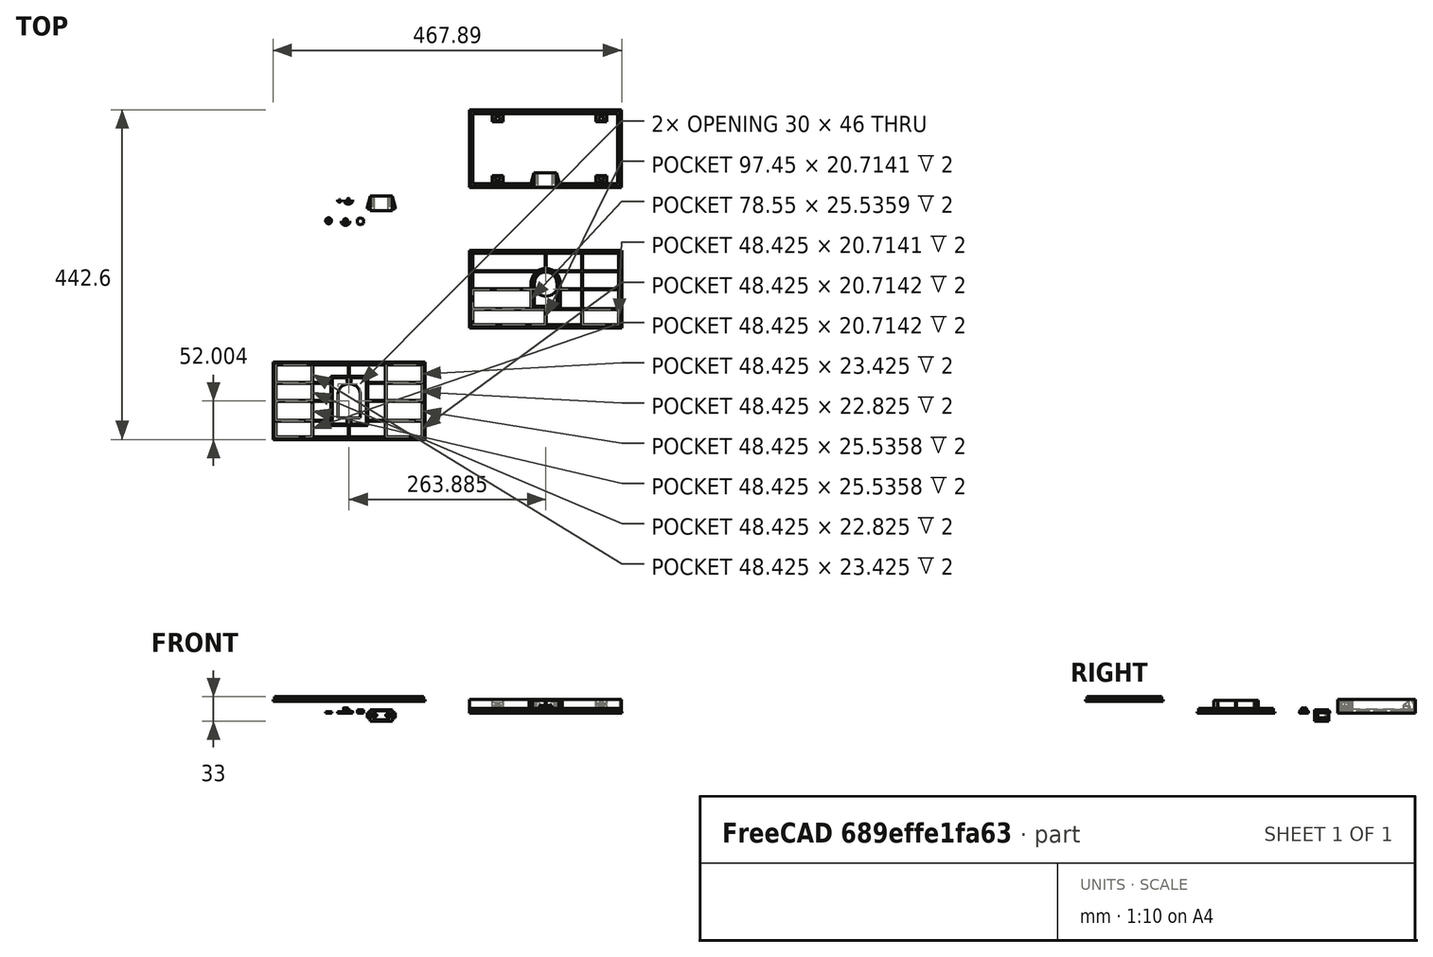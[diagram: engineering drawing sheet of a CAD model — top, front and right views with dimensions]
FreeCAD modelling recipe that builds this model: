
FCSTD DOCUMENT  (FreeCAD 0.18.3R)
Label: lamp.base.template
License: All rights reserved
LicenseURL: http://en.wikipedia.org/wiki/All_rights_reserved
objects: Part::Extrusion×114, Part::Part2DObjectPython×79, Part::Cut×50, Part::MultiFuse×34, Part::Feature×31, Part::Cone×2
note: 310 computed .brp shape members not serialized (recipe doc carries the construction recipe); baked Part::Feature solids carry a one-line shape summary decoded from their .brp

FEATURE [Part::Part2DObjectPython] Rectangle071  # Draft 2D object (typed FeaturePython)
  ChamferSize = 0
  Columns = 1
  FilletRadius = 0
  Height = 100.5
  Length = 200.5
  MakeFace = true
  Placement = pos=(-212.48,-326.495,-1) rot=(0,0,1;0rad)
  Rows = 1
FEATURE [Part::Part2DObjectPython] Rectangle072  # Draft 2D object (typed FeaturePython)
  ChamferSize = 0
  Columns = 1
  FilletRadius = 0
  Height = 104
  Length = 204
  MakeFace = true
  Placement = pos=(-214.23,-328.245,-1) rot=(0,0,1;0rad)
  Rows = 1
  Support = -> [Rectangle071]
FEATURE [Part::Extrusion] Extrude098
  Base = -> Rectangle071
  Dir = (0,2e-16,1)
  DirMode = 2
  FaceMakerClass = Part::FaceMakerBullseye
  LengthFwd = 16
  LengthRev = 0
  Solid = false
  Symmetric = false
FEATURE [Part::Extrusion] Extrude099
  Base = -> Rectangle072
  Dir = (0,2e-16,1)
  DirMode = 2
  FaceMakerClass = Part::FaceMakerBullseye
  LengthFwd = 16
  LengthRev = 0
  Solid = false
  Symmetric = false
FEATURE [Part::Cut] Cut027
  Base = -> Extrude099
  Tool = -> Extrude098
FEATURE [Part::Part2DObjectPython] Rectangle073  # Draft 2D object (typed FeaturePython)
  ChamferSize = 0
  Columns = 1
  FilletRadius = 0
  Height = 100.5
  Length = 200.5
  MakeFace = true
  Placement = pos=(-212.48,-326.495,-1) rot=(0,0,1;0rad)
  Rows = 1
FEATURE [Part::Extrusion] Extrude100
  Base = -> Rectangle073
  Dir = (0,2e-16,1)
  DirMode = 2
  FaceMakerClass = Part::FaceMakerBullseye
  LengthFwd = 2
  LengthRev = 0
  Placement = pos=(0,0,1) rot=(0,0,1;0rad)
  Solid = false
  Symmetric = false
FEATURE [Part::Part2DObjectPython] Rectangle074  # Draft 2D object (typed FeaturePython)
  ChamferSize = 0
  Columns = 1
  FilletRadius = 0
  Height = 96
  Length = 196
  MakeFace = true
  Placement = pos=(-210.23,-324.245,4.41e-14) rot=(0,0,1;0rad)
  Rows = 1
FEATURE [Part::Extrusion] Extrude101
  Base = -> Rectangle074
  Dir = (0,2e-16,1)
  DirMode = 2
  FaceMakerClass = Part::FaceMakerBullseye
  LengthFwd = 10
  LengthRev = 0
  Solid = false
  Symmetric = false
FEATURE [Part::Cut] Cut028
  Base = -> Extrude100
  Tool = -> Extrude101
FEATURE [Part::Feature] Face
  shape: bbox 204 x 104 x 2e-07 mm, 1 faces, 0 solids (baked)
FEATURE [Part::Extrusion] Extrusion001
  Base = -> Face
  Dir = (0,-5e-16,-2)
  DirMode = 0
  FaceMakerClass = Part::FaceMakerBullseye
  LengthFwd = 0
  LengthRev = 0
  Solid = true
  Symmetric = false
FEATURE [Part::Feature] Face001
  shape: bbox 3e-07 x 96 x 2 mm, 1 faces, 0 solids (baked)
FEATURE [Part::Extrusion] Extrusion002
  Base = -> Face001
  Dir = (1,0,0)
  DirMode = 0
  FaceMakerClass = Part::FaceMakerBullseye
  LengthFwd = 0
  LengthRev = 0
  Solid = true
  Symmetric = false
FEATURE [Part::Feature] Face002
  shape: bbox 196 x 3e-07 x 2 mm, 1 faces, 0 solids (baked)
FEATURE [Part::Extrusion] Extrusion003
  Base = -> Face002
  Dir = (0,1,-2e-16)
  DirMode = 0
  FaceMakerClass = Part::FaceMakerBullseye
  LengthFwd = 0
  LengthRev = 0
  Solid = true
  Symmetric = false
FEATURE [Part::Feature] Face003
  shape: bbox 3e-07 x 96 x 2 mm, 1 faces, 0 solids (baked)
FEATURE [Part::Extrusion] Extrusion004
  Base = -> Face003
  Dir = (-1,0,0)
  DirMode = 0
  FaceMakerClass = Part::FaceMakerBullseye
  LengthFwd = 0
  LengthRev = 0
  Solid = true
  Symmetric = false
FEATURE [Part::Feature] Face004
  shape: bbox 196 x 3e-07 x 2 mm, 1 faces, 0 solids (baked)
FEATURE [Part::Extrusion] Extrusion005
  Base = -> Face004
  Dir = (0,-1,2e-16)
  DirMode = 0
  FaceMakerClass = Part::FaceMakerBullseye
  LengthFwd = 0
  LengthRev = 0
  Solid = true
  Symmetric = false
FEATURE [Part::MultiFuse] Fusion022
  Shapes = -> [Extrusion003,Extrusion004,Extrusion002,Extrusion005]
FEATURE [Part::MultiFuse] Fusion023
  Shapes = -> [Extrusion001,Cut027]
FEATURE [Part::MultiFuse] Fusion024
  Shapes = -> [Fusion023,Fusion022]
FEATURE [Part::Part2DObjectPython] Rectangle085  # Draft 2D object (typed FeaturePython)
  ChamferSize = 0
  Columns = 1
  FilletRadius = 0
  Height = 96.1
  Length = 196.1
  MakeFace = true
  Placement = pos=(-211.308,-540.059,-3) rot=(0,0,1;0rad)
  Rows = 1
FEATURE [Part::Part2DObjectPython] Rectangle086  # Draft 2D object (typed FeaturePython)
  ChamferSize = 0
  Columns = 1
  FilletRadius = 0
  Height = 104
  Length = 204
  MakeFace = true
  Placement = pos=(-215.258,-544.009,-3) rot=(0,0,1;0rad)
  Rows = 1
FEATURE [Part::Extrusion] Extrude120
  Base = -> Rectangle086
  Dir = (0,2e-16,1)
  DirMode = 2
  FaceMakerClass = Part::FaceMakerBullseye
  LengthFwd = 2
  LengthRev = 0
  Placement = pos=(-4.3e-14,5.7e-14,-6) rot=(0,0,1;0rad)
  Solid = false
  Symmetric = false
FEATURE [Part::Part2DObjectPython] Rectangle087  # Draft 2D object (typed FeaturePython)
  ChamferSize = 0
  Columns = 1
  FilletRadius = 0
  Height = 100.1
  Length = 200.1
  MakeFace = true
  Placement = pos=(-213.308,-542.059,-3) rot=(0,0,1;0rad)
  Rows = 1
  Support = -> [Rectangle085]
FEATURE [Part::Extrusion] Extrude121
  Base = -> Rectangle087
  Dir = (0,0,1)
  DirMode = 2
  FaceMakerClass = Part::FaceMakerBullseye
  LengthFwd = -4
  LengthRev = 0
  Solid = false
  Symmetric = false
FEATURE [Part::Extrusion] Extrude122
  Base = -> Rectangle085
  Dir = (0,0,1)
  DirMode = 2
  FaceMakerClass = Part::FaceMakerBullseye
  LengthFwd = -4
  LengthRev = 0
  Solid = false
  Symmetric = false
FEATURE [Part::Cut] Cut035
  Base = -> Extrude121
  Tool = -> Extrude122
FEATURE [Part::Part2DObjectPython] Rectangle088  # Draft 2D object (typed FeaturePython)
  ChamferSize = 0
  Columns = 1
  FilletRadius = 0
  Height = 1.2
  Length = 196.1
  MakeFace = true
  Placement = pos=(-211.308,-492.009,-3) rot=(0,0,1;0rad)
  Rows = 1
FEATURE [Part::Part2DObjectPython] Rectangle089  # Draft 2D object (typed FeaturePython)
  ChamferSize = 0
  Columns = 1
  FilletRadius = 0
  Height = 96.1
  Length = 1.2
  MakeFace = true
  Placement = pos=(-113.858,-443.959,-3) rot=(1,0,0;3.14159rad)
  Rows = 1
  Support = -> [Cut035]
FEATURE [Part::Part2DObjectPython] Rectangle090  # Draft 2D object (typed FeaturePython)
  ChamferSize = 0
  Columns = 1
  FilletRadius = 0
  Height = 1.2
  Length = 196.1
  MakeFace = true
  Placement = pos=(-211.308,-467.384,-3) rot=(1,0,0;3.14159rad)
  Rows = 1
FEATURE [Part::Part2DObjectPython] Rectangle091  # Draft 2D object (typed FeaturePython)
  ChamferSize = 0
  Columns = 1
  FilletRadius = 0
  Height = 1.2
  Length = 196.1
  MakeFace = true
  Placement = pos=(-211.308,-518.145,-3) rot=(1,0,0;3.14159rad)
  Rows = 1
FEATURE [Part::Part2DObjectPython] Rectangle092  # Draft 2D object (typed FeaturePython)
  ChamferSize = 0
  Columns = 1
  FilletRadius = 0
  Height = 96.1
  Length = 1.2
  MakeFace = true
  Placement = pos=(-64.8332,-443.959,-3) rot=(1,0,0;3.14159rad)
  Rows = 1
FEATURE [Part::Extrusion] Extrude123
  Base = -> Rectangle090
  Dir = (0,-2e-16,-1)
  DirMode = 2
  FaceMakerClass = Part::FaceMakerBullseye
  LengthFwd = 2
  LengthRev = 0
  Placement = pos=(-2.8e-14,0,-2) rot=(0,0,1;0rad)
  Solid = false
  Symmetric = false
FEATURE [Part::Extrusion] Extrude124
  Base = -> Rectangle092
  Dir = (0,-2e-16,-1)
  DirMode = 2
  FaceMakerClass = Part::FaceMakerBullseye
  LengthFwd = 2
  LengthRev = 0
  Placement = pos=(-2.8e-14,0,-2) rot=(0,0,1;0rad)
  Solid = false
  Symmetric = false
FEATURE [Part::Extrusion] Extrude125
  Base = -> Rectangle088
  Dir = (0,2e-16,1)
  DirMode = 2
  FaceMakerClass = Part::FaceMakerBullseye
  LengthFwd = -2
  LengthRev = 0
  Placement = pos=(-2.8e-14,-0.6,-2) rot=(0,0,1;0rad)
  Solid = false
  Symmetric = false
FEATURE [Part::Extrusion] Extrude126
  Base = -> Rectangle091
  Dir = (0,-2e-16,-1)
  DirMode = 2
  FaceMakerClass = Part::FaceMakerBullseye
  LengthFwd = 2
  LengthRev = 0
  Placement = pos=(-2.8e-14,0,-2) rot=(0,0,1;0rad)
  Solid = false
  Symmetric = false
FEATURE [Part::Extrusion] Extrude127
  Base = -> Rectangle089
  Dir = (0,0,-1)
  DirMode = 2
  FaceMakerClass = Part::FaceMakerBullseye
  LengthFwd = 2
  LengthRev = 0
  Placement = pos=(-2.8e-14,0,-2) rot=(0,0,1;0rad)
  Solid = false
  Symmetric = false
FEATURE [Part::Part2DObjectPython] Circle022  # Draft 2D object (typed FeaturePython)
  FirstAngle = 0
  LastAngle = 0
  MakeFace = true
  Placement = pos=(-130.429,-169.951,7.33959) rot=(1,0,0;3.14157rad)
  Radius = 6
FEATURE [Part::Part2DObjectPython] Circle023  # Draft 2D object (typed FeaturePython)
  FirstAngle = 0
  LastAngle = 0
  MakeFace = true
  Placement = pos=(-130.429,-169.951,7.33959) rot=(-1,0,0;2.2e-05rad)
  Radius = 2.5
FEATURE [Part::Part2DObjectPython] Circle  # Draft 2D object (typed FeaturePython)
  FirstAngle = 0
  LastAngle = 0
  MakeFace = true
  Placement = pos=(-130.429,-169.95,12.3396) rot=(-1,0,0;2.2e-05rad)
  Radius = 3
FEATURE [Part::Extrusion] Extrude142
  Base = -> Circle
  Dir = (0,2.19278e-05,1)
  DirMode = 2
  FaceMakerClass = Part::FaceMakerBullseye
  LengthFwd = -2.5
  LengthRev = 0
  Solid = false
  Symmetric = false
FEATURE [Part::Part2DObjectPython] Rectangle104  # Draft 2D object (typed FeaturePython)
  ChamferSize = 0
  Columns = 1
  FilletRadius = 0
  Height = 2
  Length = 6
  MakeFace = true
  Placement = pos=(-133.429,-170.95,12.3396) rot=(-1,0,0;2.2e-05rad)
  Rows = 1
  Support = -> [Extrude142]
FEATURE [Part::Cone] Cone002
  Angle = 360
  AttacherType = Attacher::AttachEngine3D
  Height = 10
  Placement = pos=(-126.434,-151.902,12.3392) rot=(0,0,1;0rad)
  Radius1 = 6
  Radius2 = 3
FEATURE [Part::Cone] Cone
  Angle = 360
  AttacherType = Attacher::AttachEngine3D
  Height = 10
  Placement = pos=(-126.434,-151.902,12.3392) rot=(0,0,1;0rad)
  Radius1 = 5
  Radius2 = 0
FEATURE [Part::Cut] Cut048
  Base = -> Cone002
  Placement = pos=(-3.99517,-18.0483,-4.4996) rot=(0,0,1;0rad)
  Tool = -> Cone
FEATURE [Part::Part2DObjectPython] Wire005  # Draft 2D object (typed FeaturePython)
  ChamferSize = 0
  Closed = true
  End = (-172.23,-313.495,6)
  FilletRadius = 0
  Length = 29.8885
  MakeFace = true
  Placement = pos=(-176.23,-311.495,6) rot=(0,0,1;0rad)
  Points = (6) [(0,0,0),(-4,-2,-1.77636e-15),(-4,-8,0),(0,-10,0),(4,-8,8.88178e-16),(4,-2,1.77636e-15)]
  Start = (-176.23,-311.495,6)
  Subdivisions = 0
FEATURE [Part::Extrusion] Extrude148
  Base = -> Wire005
  Dir = (0,0,1)
  DirMode = 2
  FaceMakerClass = Part::FaceMakerBullseye
  LengthFwd = 4.4
  LengthRev = 0
  Placement = pos=(139.25,80.4695,-4) rot=(0,0,1;0rad)
  Solid = false
  Symmetric = false
FEATURE [Part::Part2DObjectPython] Rectangle  # Draft 2D object (typed FeaturePython)
  ChamferSize = 0
  Columns = 1
  FilletRadius = 0
  Height = 14
  Length = 15
  MakeFace = true
  Placement = pos=(-183.73,-326.495,6) rot=(0,0,1;0rad)
  Rows = 1
FEATURE [Part::Extrusion] Extrude149
  Base = -> Wire005
  Dir = (0,0,1)
  DirMode = 2
  FaceMakerClass = Part::FaceMakerBullseye
  LengthFwd = 4.4
  LengthRev = 0
  Placement = pos=(71.3743,-83.0439,-15) rot=(0,0,1;0rad)
  Solid = false
  Symmetric = false
FEATURE [Part::Extrusion] Extrude150
  Base = -> Wire005
  Dir = (0,0,1)
  DirMode = 2
  FaceMakerClass = Part::FaceMakerBullseye
  LengthFwd = 4.4
  LengthRev = 0
  Placement = pos=(-2.8e-14,0,-4) rot=(0,0,1;0rad)
  Solid = false
  Symmetric = false
FEATURE [Part::Extrusion] Extrude151
  Base = -> Wire005
  Dir = (0,0,1)
  DirMode = 2
  FaceMakerClass = Part::FaceMakerBullseye
  LengthFwd = 4.4
  LengthRev = 0
  Placement = pos=(-2.8e-14,80.4695,-4) rot=(0,0,1;0rad)
  Solid = false
  Symmetric = false
FEATURE [Part::Extrusion] Extrude152
  Base = -> Wire005
  Dir = (0,0,1)
  DirMode = 2
  FaceMakerClass = Part::FaceMakerBullseye
  LengthFwd = 4.4
  LengthRev = 0
  Placement = pos=(139.25,0,-4) rot=(0,0,1;0rad)
  Solid = false
  Symmetric = false
FEATURE [Part::Part2DObjectPython] Circle024  # Draft 2D object (typed FeaturePython)
  FirstAngle = 0
  LastAngle = 0
  MakeFace = true
  Placement = pos=(-176.23,-316.495,1.32e-13) rot=(1,0,0;3.14159rad)
  Radius = 2.8
FEATURE [Part::Extrusion] Extrude
  Base = -> Circle024
  Dir = (0,0,-1)
  DirMode = 2
  FaceMakerClass = Part::FaceMakerBullseye
  LengthFwd = -6.4
  LengthRev = 0
  Solid = false
  Symmetric = false
FEATURE [Part::Part2DObjectPython] Circle025  # Draft 2D object (typed FeaturePython)
  FirstAngle = 0
  LastAngle = 0
  MakeFace = true
  Placement = pos=(-176.23,-236.025,2.3e-14) rot=(1,0,0;3.14159rad)
  Radius = 2.8
  Support = -> [Extrude]
FEATURE [Part::Extrusion] Extrude153
  Base = -> Circle025
  Dir = (0,0,-1)
  DirMode = 2
  FaceMakerClass = Part::FaceMakerBullseye
  LengthFwd = -6.4
  LengthRev = 0
  Solid = false
  Symmetric = false
FEATURE [Part::Part2DObjectPython] Circle026  # Draft 2D object (typed FeaturePython)
  FirstAngle = 0
  LastAngle = 0
  MakeFace = true
  Placement = pos=(-36.9799,-316.495,2.5e-14) rot=(1,0,0;3.14159rad)
  Radius = 2.8
FEATURE [Part::Extrusion] Extrude154
  Base = -> Circle026
  Dir = (0,0,-1)
  DirMode = 2
  FaceMakerClass = Part::FaceMakerBullseye
  LengthFwd = -6.4
  LengthRev = 0
  Solid = false
  Symmetric = false
FEATURE [Part::Part2DObjectPython] Circle027  # Draft 2D object (typed FeaturePython)
  FirstAngle = 0
  LastAngle = 0
  MakeFace = true
  Placement = pos=(-36.9799,-236.025,2.5e-14) rot=(1,0,0;3.14159rad)
  Radius = 2.8
FEATURE [Part::Extrusion] Extrude155
  Base = -> Circle027
  Dir = (0,0,-1)
  DirMode = 2
  FaceMakerClass = Part::FaceMakerBullseye
  LengthFwd = -6.4
  LengthRev = 0
  Solid = false
  Symmetric = false
FEATURE [Part::Part2DObjectPython] Rectangle105  # Draft 2D object (typed FeaturePython)
  ChamferSize = 0
  Columns = 1
  FilletRadius = 0
  Height = 14
  Length = 15
  MakeFace = true
  Placement = pos=(-44.4799,-326.495,6) rot=(0,0,1;0rad)
  Rows = 1
FEATURE [Part::Part2DObjectPython] Rectangle106  # Draft 2D object (typed FeaturePython)
  ChamferSize = 0
  Columns = 1
  FilletRadius = 0
  Height = 14.0305
  Length = 15
  MakeFace = true
  Placement = pos=(-44.4799,-240.025,6) rot=(0,0,1;0rad)
  Rows = 1
FEATURE [Part::Part2DObjectPython] Rectangle107  # Draft 2D object (typed FeaturePython)
  ChamferSize = 0
  Columns = 1
  FilletRadius = 0
  Height = 14.0305
  Length = 15
  MakeFace = true
  Placement = pos=(-183.73,-240.025,6) rot=(0,0,1;0rad)
  Rows = 1
FEATURE [Part::Extrusion] Extrude156
  Base = -> Rectangle106
  Dir = (0,0,1)
  DirMode = 2
  FaceMakerClass = Part::FaceMakerBullseye
  LengthFwd = -6.4
  LengthRev = 0
  Placement = pos=(0,0,0.4) rot=(0,0,1;0rad)
  Solid = false
  Symmetric = false
FEATURE [Part::Extrusion] Extrude157
  Base = -> Rectangle107
  Dir = (0,0,1)
  DirMode = 2
  FaceMakerClass = Part::FaceMakerBullseye
  LengthFwd = -6.4
  LengthRev = 0
  Placement = pos=(0,0,0.4) rot=(0,0,1;0rad)
  Solid = false
  Symmetric = false
FEATURE [Part::Extrusion] Extrude158
  Base = -> Rectangle
  Dir = (0,0,1)
  DirMode = 2
  FaceMakerClass = Part::FaceMakerBullseye
  LengthFwd = -6.4
  LengthRev = 0
  Placement = pos=(0,0,0.4) rot=(0,0,1;0rad)
  Solid = false
  Symmetric = false
FEATURE [Part::Extrusion] Extrude159
  Base = -> Rectangle105
  Dir = (0,0,1)
  DirMode = 2
  FaceMakerClass = Part::FaceMakerBullseye
  LengthFwd = -6.4
  LengthRev = 0
  Placement = pos=(0,0,0.4) rot=(0,0,1;0rad)
  Solid = false
  Symmetric = false
FEATURE [Part::Cut] Cut050
  Base = -> Extrude159
  Tool = -> Extrude152
FEATURE [Part::Cut] Cut051
  Base = -> Cut050
  Tool = -> Extrude154
FEATURE [Part::Cut] Cut052
  Base = -> Extrude158
  Tool = -> Extrude150
FEATURE [Part::Cut] Cut053
  Base = -> Cut052
  Tool = -> Extrude
FEATURE [Part::Cut] Cut054
  Base = -> Extrude157
  Tool = -> Extrude151
FEATURE [Part::Cut] Cut055
  Base = -> Cut054
  Tool = -> Extrude153
FEATURE [Part::Cut] Cut056
  Base = -> Extrude156
  Tool = -> Extrude148
FEATURE [Part::Cut] Cut057
  Base = -> Cut056
  Tool = -> Extrude155
FEATURE [Part::Part2DObjectPython] Rectangle108  # Draft 2D object (typed FeaturePython)
  ChamferSize = 0
  Columns = 1
  FilletRadius = 0
  Height = 4.4
  Length = 8
  MakeFace = true
  Placement = pos=(-32.9799,-239.025,2) rot=(0,0.707107,0.707107;3.14159rad)
  Rows = 1
  Support = -> [Fusion024]
FEATURE [Part::Part2DObjectPython] Rectangle109  # Draft 2D object (typed FeaturePython)
  ChamferSize = 0
  Columns = 1
  FilletRadius = 0
  Height = 4.4
  Length = 8
  MakeFace = true
  Placement = pos=(-172.23,-239.025,2) rot=(0,0.707107,0.707107;3.14159rad)
  Rows = 1
FEATURE [Part::Part2DObjectPython] Rectangle110  # Draft 2D object (typed FeaturePython)
  ChamferSize = 0
  Columns = 1
  FilletRadius = 0
  Height = 4.4
  Length = 8
  MakeFace = true
  Placement = pos=(-172.23,-313.495,2) rot=(0,0.707107,0.707107;3.14159rad)
  Rows = 1
FEATURE [Part::Part2DObjectPython] Rectangle111  # Draft 2D object (typed FeaturePython)
  ChamferSize = 0
  Columns = 1
  FilletRadius = 0
  Height = 4.4
  Length = 8
  MakeFace = true
  Placement = pos=(-32.9799,-313.495,2) rot=(0,0.707107,0.707107;3.14159rad)
  Rows = 1
FEATURE [Part::Extrusion] Extrude160
  Base = -> Rectangle111
  Dir = (0,1,-2e-16)
  DirMode = 2
  FaceMakerClass = Part::FaceMakerBullseye
  LengthFwd = 8
  LengthRev = 0
  Solid = false
  Symmetric = false
FEATURE [Part::Cut] Cut058
  Base = -> Cut051
  Tool = -> Extrude160
FEATURE [Part::Extrusion] Extrude161
  Base = -> Rectangle110
  Dir = (0,1,-2e-16)
  DirMode = 2
  FaceMakerClass = Part::FaceMakerBullseye
  LengthFwd = 8
  LengthRev = 0
  Solid = false
  Symmetric = false
FEATURE [Part::Cut] Cut059
  Base = -> Cut053
  Tool = -> Extrude161
FEATURE [Part::Extrusion] Extrude162
  Base = -> Rectangle109
  Dir = (0,1,-2e-16)
  DirMode = 2
  FaceMakerClass = Part::FaceMakerBullseye
  LengthFwd = -8
  LengthRev = 0
  Solid = false
  Symmetric = false
FEATURE [Part::Cut] Cut060
  Base = -> Cut055
  Tool = -> Extrude162
FEATURE [Part::Extrusion] Extrude163
  Base = -> Rectangle108
  Dir = (0,1,-2e-16)
  DirMode = 2
  FaceMakerClass = Part::FaceMakerBullseye
  LengthFwd = -8
  LengthRev = 0
  Solid = false
  Symmetric = false
FEATURE [Part::Cut] Cut061
  Base = -> Cut057
  Tool = -> Extrude163
FEATURE [Part::Part2DObjectPython] Rectangle112  # Draft 2D object (typed FeaturePython)
  ChamferSize = 0
  Columns = 1
  FilletRadius = 0
  Height = 14.0305
  Length = 15
  MakeFace = true
  Placement = pos=(-44.4799,-240.025,6.4) rot=(0,0,1;0rad)
  Rows = 1
  Support = -> [Cut061]
FEATURE [Part::Part2DObjectPython] Rectangle113  # Draft 2D object (typed FeaturePython)
  ChamferSize = 0
  Columns = 1
  FilletRadius = 0
  Height = 14.0305
  Length = 15
  MakeFace = true
  Placement = pos=(-183.73,-240.025,6.4) rot=(0,0,1;0rad)
  Rows = 1
FEATURE [Part::Part2DObjectPython] Rectangle114  # Draft 2D object (typed FeaturePython)
  ChamferSize = 0
  Columns = 1
  FilletRadius = 0
  Height = 14
  Length = 15
  MakeFace = true
  Placement = pos=(-44.4799,-326.495,6.4) rot=(0,0,1;0rad)
  Rows = 1
FEATURE [Part::Part2DObjectPython] Rectangle115  # Draft 2D object (typed FeaturePython)
  ChamferSize = 0
  Columns = 1
  FilletRadius = 0
  Height = 14
  Length = 15
  MakeFace = true
  Placement = pos=(-183.73,-326.495,6.4) rot=(0,0,1;0rad)
  Rows = 1
FEATURE [Part::Extrusion] Extrude164
  Base = -> Rectangle114
  Dir = (0,0,1)
  DirMode = 2
  FaceMakerClass = Part::FaceMakerBullseye
  LengthFwd = 1
  LengthRev = 0
  Solid = false
  Symmetric = false
FEATURE [Part::Extrusion] Extrude165
  Base = -> Rectangle115
  Dir = (0,0,1)
  DirMode = 2
  FaceMakerClass = Part::FaceMakerBullseye
  LengthFwd = 1
  LengthRev = 0
  Solid = false
  Symmetric = false
FEATURE [Part::Extrusion] Extrude166
  Base = -> Rectangle113
  Dir = (0,0,1)
  DirMode = 2
  FaceMakerClass = Part::FaceMakerBullseye
  LengthFwd = 1
  LengthRev = 0
  Solid = false
  Symmetric = false
FEATURE [Part::Extrusion] Extrude167
  Base = -> Rectangle112
  Dir = (0,0,1)
  DirMode = 2
  FaceMakerClass = Part::FaceMakerBullseye
  LengthFwd = 1
  LengthRev = 0
  Solid = false
  Symmetric = false
FEATURE [Part::Feature] Face005
  Placement = pos=(-183.73,-326.495,7.4) rot=(0,0,1;0rad)
  shape: bbox 15 x 14 x 2e-07 mm, 1 faces, 0 solids (baked)
FEATURE [Part::Extrusion] Extrusion
  Base = -> Face005
  Dir = (-2e-16,-2e-16,7.6)
  DirMode = 0
  FaceMakerClass = Part::FaceMakerBullseye
  LengthFwd = 0
  LengthRev = 0
  Solid = true
  Symmetric = false
FEATURE [Part::Feature] Face006
  Placement = pos=(-44.4799,-326.495,7.4) rot=(0,0,1;0rad)
  shape: bbox 15 x 14 x 2e-07 mm, 1 faces, 0 solids (baked)
FEATURE [Part::Extrusion] Extrusion006
  Base = -> Face006
  Dir = (-2e-16,-2e-16,7.6)
  DirMode = 0
  FaceMakerClass = Part::FaceMakerBullseye
  LengthFwd = 0
  LengthRev = 0
  Solid = true
  Symmetric = false
FEATURE [Part::Feature] Face007
  Placement = pos=(-183.73,-240.025,7.4) rot=(0,0,1;0rad)
  shape: bbox 15 x 14.03 x 2e-07 mm, 1 faces, 0 solids (baked)
FEATURE [Part::Extrusion] Extrusion007
  Base = -> Face007
  Dir = (-2e-16,-2e-16,7.6)
  DirMode = 0
  FaceMakerClass = Part::FaceMakerBullseye
  LengthFwd = 0
  LengthRev = 0
  Solid = true
  Symmetric = false
FEATURE [Part::Feature] Face008
  Placement = pos=(-44.4799,-240.025,7.4) rot=(0,0,1;0rad)
  shape: bbox 15 x 14.03 x 2e-07 mm, 1 faces, 0 solids (baked)
FEATURE [Part::Extrusion] Extrusion008
  Base = -> Face008
  Dir = (-2e-16,-2e-16,7.6)
  DirMode = 0
  FaceMakerClass = Part::FaceMakerBullseye
  LengthFwd = 0
  LengthRev = 0
  Solid = true
  Symmetric = false
FEATURE [Part::Part2DObjectPython] Wire006  # Draft 2D object (typed FeaturePython)
  ChamferSize = 0
  Closed = true
  End = (-29.4799,-240.025,7.4)
  FilletRadius = 0
  Length = 28.4334
  MakeFace = true
  Placement = pos=(-29.4799,-230.995,15) rot=(0.57735,0.57735,0.57735;2.0944rad)
  Points = (3) [(0,0,0),(-9.03045,0,0),(-9.03045,-7.6,0)]
  Start = (-29.4799,-230.995,15)
  Subdivisions = 0
  Support = -> [Extrusion008]
FEATURE [Part::Extrusion] Extrude168
  Base = -> Wire006
  Dir = (1,0,0)
  DirMode = 2
  FaceMakerClass = Part::FaceMakerBullseye
  LengthFwd = -180
  LengthRev = 0
  Solid = false
  Symmetric = false
FEATURE [Part::Part2DObjectPython] Wire007  # Draft 2D object (typed FeaturePython)
  ChamferSize = 0
  Closed = true
  End = (-183.73,-240.025,7.4)
  FilletRadius = 0
  Length = 28.4334
  MakeFace = true
  Placement = pos=(-183.73,-230.995,15) rot=(0,0,1;0rad)
  Points = (3) [(0,0,0),(0,-9.03045,0),(0,-9.03045,-7.6)]
  Start = (-183.73,-230.995,15)
  Subdivisions = 0
  Support = -> [Extrude168]
FEATURE [Part::Extrusion] Extrude169
  Base = -> Wire007
  Dir = (-15,0,0)
  DirLink = -> Extrusion007 [Edge4]
  DirMode = 1
  FaceMakerClass = Part::FaceMakerBullseye
  LengthFwd = -160
  LengthRev = 0
  Solid = false
  Symmetric = false
FEATURE [Part::Cut] Cut062
  Base = -> Extrusion008
  Tool = -> Extrude169
FEATURE [Part::Cut] Cut063
  Base = -> Extrusion007
  Tool = -> Extrude168
FEATURE [Part::Part2DObjectPython] Wire008  # Draft 2D object (typed FeaturePython)
  ChamferSize = 0
  Closed = true
  End = (-183.73,-312.495,7.4)
  FilletRadius = 0
  Length = 28.3796
  MakeFace = true
  Placement = pos=(-183.73,-321.495,15) rot=(0,0,1;0rad)
  Points = (3) [(0,0,0),(0,9,0),(0,9,-7.6)]
  Start = (-183.73,-321.495,15)
  Subdivisions = 0
FEATURE [Part::Extrusion] Extrude170
  Base = -> Wire008
  Dir = (15,0,0)
  DirLink = -> Extrusion [Edge10]
  DirMode = 1
  FaceMakerClass = Part::FaceMakerBullseye
  LengthFwd = 160
  LengthRev = 0
  Solid = false
  Symmetric = false
FEATURE [Part::Part2DObjectPython] Wire009  # Draft 2D object (typed FeaturePython)
  ChamferSize = 0
  Closed = true
  End = (-29.4799,-312.495,7.4)
  FilletRadius = 0
  Length = 28.3796
  MakeFace = true
  Placement = pos=(-29.4799,-321.495,15) rot=(0,0,1;0rad)
  Points = (3) [(0,0,0),(0,9,1.77636e-15),(0,9,-7.6)]
  Start = (-29.4799,-321.495,15)
  Subdivisions = 0
FEATURE [Part::Extrusion] Extrude171
  Base = -> Wire009
  Dir = (15,0,0)
  DirLink = -> Extrusion006 [Edge10]
  DirMode = 1
  FaceMakerClass = Part::FaceMakerBullseye
  LengthFwd = -160
  LengthRev = 0
  Solid = false
  Symmetric = false
FEATURE [Part::Cut] Cut064
  Base = -> Extrusion
  Tool = -> Extrude171
FEATURE [Part::Cut] Cut065
  Base = -> Extrusion006
  Tool = -> Extrude170
FEATURE [Part::MultiFuse] Fusion
  Shapes = -> [Cut060,Extrude166,Cut063]
FEATURE [Part::MultiFuse] Fusion032
  Shapes = -> [Cut061,Extrude167,Cut062]
FEATURE [Part::MultiFuse] Fusion033
  Shapes = -> [Cut059,Extrude165,Cut064]
FEATURE [Part::MultiFuse] Fusion034
  Shapes = -> [Cut058,Extrude164,Cut065]
FEATURE [Part::MultiFuse] Fusion035
  Shapes = -> [Fusion034,Fusion033,Fusion032,Fusion]
FEATURE [Part::Part2DObjectPython] Rectangle116  # Draft 2D object (typed FeaturePython)
  ChamferSize = 0
  Columns = 1
  FilletRadius = 0
  Height = 2
  Length = 200.5
  MakeFace = true
  Placement = pos=(-212.48,-326.495,15) rot=(0,0,1;0rad)
  Rows = 1
FEATURE [Part::Extrusion] Extrude172
  Base = -> Rectangle116
  Dir = (0,0,1)
  DirMode = 2
  FaceMakerClass = Part::FaceMakerBullseye
  LengthFwd = -4
  LengthRev = 0
  Solid = false
  Symmetric = false
FEATURE [Part::Cut] Cut066
  Base = -> Fusion035
  Tool = -> Extrude172
FEATURE [Part::Part2DObjectPython] Rectangle117  # Draft 2D object (typed FeaturePython)
  ChamferSize = 0
  Columns = 1
  FilletRadius = 0
  Height = 2
  Length = 200.5
  MakeFace = true
  Placement = pos=(-212.48,-227.995,15) rot=(0,0,1;0rad)
  Rows = 1
FEATURE [Part::Extrusion] Extrude173
  Base = -> Rectangle117
  Dir = (0,0,1)
  DirMode = 2
  FaceMakerClass = Part::FaceMakerBullseye
  LengthFwd = -4
  LengthRev = 0
  Solid = false
  Symmetric = false
FEATURE [Part::Cut] Cut067
  Base = -> Cut066
  Tool = -> Extrude173
FEATURE [Part::MultiFuse] Fusion043
FEATURE [Part::Extrusion] Extrude143
  Base = -> Rectangle104
  Dir = (0,2.19278e-05,1)
  DirMode = 2
  FaceMakerClass = Part::FaceMakerBullseye
  LengthFwd = -4
  LengthRev = 0
  Solid = false
  Symmetric = false
FEATURE [Part::Extrusion] Extrude141
  Base = -> Circle023
  Dir = (0,2.19278e-05,1)
  DirMode = 2
  FaceMakerClass = Part::FaceMakerBullseye
  LengthFwd = 5
  LengthRev = 0
  Solid = false
  Symmetric = false
FEATURE [Part::Extrusion] Extrude140
  Base = -> Circle022
  Dir = (0,-2.19278e-05,-1)
  DirMode = 2
  FaceMakerClass = Part::FaceMakerBullseye
  LengthFwd = 2
  LengthRev = 0
  Solid = false
  Symmetric = false
FEATURE [Part::MultiFuse] Fusion031
  Shapes = -> [Extrude140,Extrude141,Extrude142]
FEATURE [Part::Cut] Cut
  Base = -> Fusion031
  Tool = -> Extrude143
FEATURE [Part::Cut] Cut049
  Base = -> Cut
  Placement = pos=(5.64319,-229.101,-14.3396) rot=(0,0,1;0rad)
  Tool = -> Cut048
FEATURE [Part::Feature] Face009
  shape: bbox 30 x 15 x 0.0003291 mm, 1 faces, 0 solids (baked)
FEATURE [Part::Extrusion] Extrusion009
  Base = -> Face009
  Dir = (0,4.38557e-05,2)
  DirMode = 0
  FaceMakerClass = Part::FaceMakerBullseye
  LengthFwd = 0
  LengthRev = 0
  Solid = true
  Symmetric = false
FEATURE [Part::Feature] Face010
  shape: bbox 30 x 15 x 0.0003291 mm, 1 faces, 0 solids (baked)
FEATURE [Part::Extrusion] Extrusion010
  Base = -> Face010
  Dir = (0,4.38557e-05,2)
  DirMode = 0
  FaceMakerClass = Part::FaceMakerBullseye
  LengthFwd = 0
  LengthRev = 0
  Solid = true
  Symmetric = false
FEATURE [Part::Feature] Face011
  shape: bbox 30 x 31 x 0.00068 mm, 1 faces, 0 solids (baked)
FEATURE [Part::Extrusion] Extrusion011
  Base = -> Face011
  Dir = (0,4.38557e-05,2)
  DirMode = 0
  FaceMakerClass = Part::FaceMakerBullseye
  LengthFwd = 0
  LengthRev = 0
  Solid = true
  Symmetric = false
FEATURE [Part::MultiFuse] Fusion045
  Placement = pos=(257.095,1.53462,5e-15) rot=(0,0,1;0rad)
  Shapes = -> [Extrude127,Extrude126,Extrude125,Extrude124,Extrude123,Extrude120,Cut035]
FEATURE [Part::MultiFuse] Fusion046
  Shapes = -> [Cut067,Fusion024]
FEATURE [Part::MultiFuse] Fusion047
  Placement = pos=(255.504,-25.6076,-6) rot=(0,0,1;0rad)
  Shapes = -> [Cut028,Fusion046]
FEATURE [Part::MultiFuse] Fusion048
  Placement = pos=(253.903,-336.034,-13.3392) rot=(0,0,1;0rad)
  Shapes = -> [Fusion043,Extrusion009,Extrusion010,Extrusion011]
FEATURE [Part::Feature] Face012
  Placement = pos=(253.903,-336.034,-13.3392) rot=(0,0,1;0rad)
  shape: bbox 30 x 31 x 0.00068 mm, 1 faces, 0 solids (baked)
FEATURE [Part::Extrusion] Extrusion012
  Base = -> Face012
  Dir = (0,0.000131567,6)
  DirMode = 0
  FaceMakerClass = Part::FaceMakerBullseye
  LengthFwd = 0
  LengthRev = 0
  Solid = true
  Symmetric = false
FEATURE [Part::MultiFuse] Fusion049
  Shapes = -> [Fusion048,Extrusion012]
FEATURE [Part::Feature] Face013
  shape: bbox 30 x 15 x 0.0003291 mm, 1 faces, 0 solids (baked)
FEATURE [Part::Extrusion] Extrusion013
  Base = -> Face013
  Dir = (0,0.000131567,6)
  DirMode = 0
  FaceMakerClass = Part::FaceMakerBullseye
  LengthFwd = 0
  LengthRev = 0
  Solid = true
  Symmetric = false
FEATURE [Part::Feature] Face014
  shape: bbox 30 x 15 x 0.0003291 mm, 1 faces, 0 solids (baked)
FEATURE [Part::Extrusion] Extrusion014
  Base = -> Face014
  Dir = (0,0.000131567,6)
  DirMode = 0
  FaceMakerClass = Part::FaceMakerBullseye
  LengthFwd = 0
  LengthRev = 0
  Solid = true
  Symmetric = false
FEATURE [Part::MultiFuse] Fusion050
  Shapes = -> [Extrusion013,Fusion049]
FEATURE [Part::Part2DObjectPython] Circle030  # Draft 2D object (typed FeaturePython)
  FirstAngle = 0
  LastAngle = 0
  MakeFace = true
  Placement = pos=(149.137,-490.474,-10) rot=(0,1,-1.1e-05;3.14159rad)
  Radius = 2.5
  Support = -> [Fusion050]
FEATURE [Part::Extrusion] Extrude176
  Base = -> Circle030
  Dir = (0,-2.19278e-05,-1)
  DirMode = 2
  FaceMakerClass = Part::FaceMakerBullseye
  LengthFwd = -10
  LengthRev = 0
  Solid = false
  Symmetric = false
FEATURE [Part::MultiFuse] Fusion051
  Shapes = -> [Fusion050,Extrude176]
FEATURE [Part::MultiFuse] Fusion052
  Shapes = -> [Extrusion014,Fusion051]
FEATURE [Part::Cut] Cut068
  Base = -> Fusion045
  Tool = -> Fusion052
FEATURE [Part::Part2DObjectPython] Circle037  # Draft 2D object (typed FeaturePython)
  FirstAngle = 0
  LastAngle = 0
  MakeFace = true
  Placement = pos=(-134.634,-362.407,-9) rot=(1,0,0;3.14159rad)
  Radius = 4
FEATURE [Part::Extrusion] Extrude187
  Base = -> Circle037
  Dir = (0,0,-1)
  DirMode = 2
  FaceMakerClass = Part::FaceMakerBullseye
  LengthFwd = -2
  LengthRev = 0
  Placement = pos=(-12.8849,-36.4288,0) rot=(0,0,1;0rad)
  Solid = false
  Symmetric = false
FEATURE [Part::Part2DObjectPython] Circle038  # Draft 2D object (typed FeaturePython)
  FirstAngle = 0
  LastAngle = 0
  MakeFace = true
  Placement = pos=(-147.519,-398.835,-7) rot=(1,0,0;3.14159rad)
  Radius = 1.5
  Support = -> [Extrude187]
FEATURE [Part::Extrusion] Extrude188
  Base = -> Circle038
  Dir = (0,0,-1)
  DirMode = 2
  FaceMakerClass = Part::FaceMakerBullseye
  LengthFwd = 3
  LengthRev = 0
  Solid = false
  Symmetric = false
FEATURE [Part::Cut] Cut076
  Base = -> Extrude187
  Tool = -> Extrude188
FEATURE [Part::Part2DObjectPython] Circle039  # Draft 2D object (typed FeaturePython)
  FirstAngle = 0
  LastAngle = 0
  MakeFace = true
  Placement = pos=(218.524,-342.102,-6) rot=(1,0,0;3.14159rad)
  Radius = 2.8
  Support = -> [Fusion047]
FEATURE [Part::Part2DObjectPython] Circle040  # Draft 2D object (typed FeaturePython)
  FirstAngle = 0
  LastAngle = 0
  MakeFace = true
  Placement = pos=(218.524,-261.633,-6) rot=(1,0,0;3.14159rad)
  Radius = 2.8
FEATURE [Part::Part2DObjectPython] Circle041  # Draft 2D object (typed FeaturePython)
  FirstAngle = 0
  LastAngle = 0
  MakeFace = true
  Placement = pos=(79.2741,-261.633,-6) rot=(1,0,0;3.14159rad)
  Radius = 2.8
FEATURE [Part::Part2DObjectPython] Circle042  # Draft 2D object (typed FeaturePython)
  FirstAngle = 0
  LastAngle = 0
  MakeFace = true
  Placement = pos=(79.2741,-342.102,-6) rot=(1,0,0;3.14159rad)
  Radius = 2.8
FEATURE [Part::Extrusion] Extrude189
  Base = -> Circle039
  Dir = (0,0,-1)
  DirMode = 2
  FaceMakerClass = Part::FaceMakerBullseye
  LengthFwd = -40
  LengthRev = 0
  Solid = false
  Symmetric = false
FEATURE [Part::Extrusion] Extrude190
  Base = -> Circle040
  Dir = (0,0,-1)
  DirMode = 2
  FaceMakerClass = Part::FaceMakerBullseye
  LengthFwd = -40
  LengthRev = 0
  Solid = false
  Symmetric = false
FEATURE [Part::Extrusion] Extrude191
  Base = -> Circle041
  Dir = (0,0,-1)
  DirMode = 2
  FaceMakerClass = Part::FaceMakerBullseye
  LengthFwd = -40
  LengthRev = 0
  Solid = false
  Symmetric = false
FEATURE [Part::Extrusion] Extrude192
  Base = -> Circle042
  Dir = (0,0,-1)
  DirMode = 2
  FaceMakerClass = Part::FaceMakerBullseye
  LengthFwd = -40
  LengthRev = 0
  Solid = false
  Symmetric = false
FEATURE [Part::MultiFuse] Fusion065
  Shapes = -> [Extrude192,Extrude189,Extrude190,Extrude191]
FEATURE [Part::Part2DObjectPython] Circle043  # Draft 2D object (typed FeaturePython)
  FirstAngle = 0
  LastAngle = 0
  MakeFace = true
  Placement = pos=(-147.519,-398.835,-7) rot=(0,0,1;0rad)
  Radius = 2
FEATURE [Part::Extrusion] Extrude193
  Base = -> Circle043
  Dir = (0,0,1)
  DirMode = 2
  FaceMakerClass = Part::FaceMakerBullseye
  LengthFwd = -1
  LengthRev = 0
  Solid = false
  Symmetric = false
FEATURE [Part::Cut] Cut078
  Base = -> Cut076
  Tool = -> Extrude193
FEATURE [Part::Feature] Face030
  shape: bbox 35 x 50.5 x 0.001108 mm, 1 faces, 0 solids (baked)
FEATURE [Part::Extrusion] Extrusion027
  Base = -> Face030
  Dir = (0,0.000372773,17)
  DirMode = 0
  FaceMakerClass = Part::FaceMakerBullseye
  LengthFwd = 0
  LengthRev = 0
  Placement = pos=(162.114,-261.462,-17) rot=(0,0,1;0rad)
  Solid = true
  Symmetric = false
FEATURE [Part::Part2DObjectPython] Rectangle132  # Draft 2D object (typed FeaturePython)
  ChamferSize = 0
  Columns = 1
  FilletRadius = 0
  Height = 12.9995
  Length = 5
  MakeFace = true
  Placement = pos=(121.337,-489.874,7.99948) rot=(-1,0,0;1.57082rad)
  Rows = 1
FEATURE [Part::Part2DObjectPython] Rectangle133  # Draft 2D object (typed FeaturePython)
  ChamferSize = 0
  Columns = 1
  FilletRadius = 0
  Height = 12.9995
  Length = 5
  MakeFace = true
  Placement = pos=(161.337,-489.874,7.99948) rot=(-1,0,0;1.57082rad)
  Rows = 1
FEATURE [Part::Extrusion] Extrusion028
  Base = -> Rectangle133
  Dir = (1.29e-14,-1.2,2.63134e-05)
  DirMode = 0
  FaceMakerClass = Part::FaceMakerBullseye
  LengthFwd = 0
  LengthRev = 0
  Solid = true
  Symmetric = false
FEATURE [Part::Extrusion] Extrusion029
  Base = -> Rectangle132
  Dir = (1.29e-14,-1.2,2.63134e-05)
  DirMode = 0
  FaceMakerClass = Part::FaceMakerBullseye
  LengthFwd = 0
  LengthRev = 0
  Solid = true
  Symmetric = false
FEATURE [Part::Part2DObjectPython] Rectangle134  # Draft 2D object (typed FeaturePython)
  ChamferSize = 0
  Columns = 1
  FilletRadius = 0
  Height = 12.9988
  Length = 5.00029
  MakeFace = true
  Placement = pos=(144.437,-465.849,-5) rot=(0.57735,0.57735,0.57735;2.0944rad)
  Rows = 1
  Support = -> [Cut068]
FEATURE [Part::Extrusion] Extrusion030
  Base = -> Rectangle134
  Dir = (-1.2,0,0)
  DirMode = 0
  FaceMakerClass = Part::FaceMakerBullseye
  LengthFwd = 0
  LengthRev = 0
  Solid = true
  Symmetric = false
FEATURE [Part::Part2DObjectPython] Rectangle135  # Draft 2D object (typed FeaturePython)
  ChamferSize = 0
  Columns = 1
  FilletRadius = 0
  Height = 17
  Length = 5.8
  MakeFace = true
  Placement = pos=(152.337,-521.821,-5.00014) rot=(0.577346,-0.577346,0.577359;2.09438rad)
  Rows = 1
  Support = -> [Extrusion027]
FEATURE [Part::Extrusion] Extrude194
  Base = -> Rectangle135
  Dir = (2.8e-15,-1,2.19278e-05)
  DirMode = 2
  FaceMakerClass = Part::FaceMakerBullseye
  LengthFwd = -20
  LengthRev = 0
  Solid = false
  Symmetric = false
FEATURE [Part::Cut] Cut079
  Base = -> Extrusion027
  Tool = -> Extrude194
FEATURE [Part::Part2DObjectPython] Rectangle136  # Draft 2D object (typed FeaturePython)
  ChamferSize = 0
  Columns = 1
  FilletRadius = 0
  Height = 1.2
  Length = 7
  MakeFace = true
  Placement = pos=(144.437,-520.474,-5) rot=(0,0,1;1.5708rad)
  Rows = 1
FEATURE [Part::Extrusion] Extrusion031
  Base = -> Rectangle136
  Dir = (-2.5e-15,-2.5e-15,12.9995)
  DirMode = 0
  FaceMakerClass = Part::FaceMakerBullseye
  LengthFwd = 0
  LengthRev = 0
  Solid = true
  Symmetric = false
FEATURE [Part::MultiFuse] Fusion066
  Shapes = -> [Cut079,Extrusion031,Extrusion028,Extrusion029,Extrusion030]
FEATURE [Part::Part2DObjectPython] Rectangle137  # Draft 2D object (typed FeaturePython)
  ChamferSize = 0
  Columns = 1
  FilletRadius = 0
  Height = 33
  Length = 35
  MakeFace = true
  Placement = pos=(126.337,-482.474,-8.99996) rot=(1,0,0;3.14159rad)
  Rows = 1
  Support = -> [Cut068]
FEATURE [Part::Part2DObjectPython] Circle044  # Draft 2D object (typed FeaturePython)
  FirstAngle = 0
  LastAngle = 0
  MakeFace = true
  Placement = pos=(143.837,-482.474,-8.99996) rot=(1,0,0;3.14159rad)
  Radius = 17.5
FEATURE [Part::Extrusion] Extrude195
  Base = -> Rectangle137
  Dir = (0,0,-1)
  DirMode = 2
  FaceMakerClass = Part::FaceMakerBullseye
  LengthFwd = -4
  LengthRev = 0
  Solid = false
  Symmetric = false
FEATURE [Part::Extrusion] Extrude196
  Base = -> Circle044
  Dir = (0,0,-1)
  DirMode = 2
  FaceMakerClass = Part::FaceMakerBullseye
  LengthFwd = -4
  LengthRev = 0
  Solid = false
  Symmetric = false
FEATURE [Part::Part2DObjectPython] Rectangle138  # Draft 2D object (typed FeaturePython)
  ChamferSize = 0
  Columns = 1
  FilletRadius = 0
  Height = 35
  Length = 39
  MakeFace = true
  Placement = pos=(124.337,-482.474,-8.99996) rot=(1,0,0;3.14159rad)
  Rows = 1
FEATURE [Part::Part2DObjectPython] Circle045  # Draft 2D object (typed FeaturePython)
  FirstAngle = 0
  LastAngle = 0
  MakeFace = true
  Placement = pos=(143.837,-482.474,-8.99996) rot=(1,0,0;3.14159rad)
  Radius = 19.5
FEATURE [Part::Extrusion] Extrude197
  Base = -> Rectangle138
  Dir = (0,0,-1)
  DirMode = 2
  FaceMakerClass = Part::FaceMakerBullseye
  LengthFwd = -4
  LengthRev = 0
  Solid = false
  Symmetric = false
FEATURE [Part::Extrusion] Extrude198
  Base = -> Circle045
  Dir = (0,0,-1)
  DirMode = 2
  FaceMakerClass = Part::FaceMakerBullseye
  LengthFwd = -4
  LengthRev = 0
  Solid = false
  Symmetric = false
FEATURE [Part::MultiFuse] Fusion067
  Shapes = -> [Extrude197,Extrude198]
FEATURE [Part::MultiFuse] Fusion068
  Shapes = -> [Extrude195,Extrude196]
FEATURE [Part::Cut] Cut080
  Base = -> Fusion067
  Tool = -> Fusion068
FEATURE [Part::MultiFuse] Fusion069
  Shapes = -> [Cut080,Fusion066]
FEATURE [Part::MultiFuse] Fusion070
  Shapes = -> [Cut068,Fusion069]
FEATURE [Part::Cut] Cut077
  Base = -> Fusion047
  Tool = -> Fusion065
FEATURE [Part::Part2DObjectPython] Rectangle150  # Draft 2D object (typed FeaturePython)
  ChamferSize = 0
  Columns = 1
  FilletRadius = 0
  Height = 12
  Length = 19
  MakeFace = true
  Placement = pos=(263.498,-353.852,-7.33221) rot=(1,0,0;1.5708rad)
  Rows = 1
  Support = -> [Cut077]
FEATURE [Part::Extrusion] Extrude224
  Base = -> Rectangle150
  Dir = (0,-1,2e-16)
  DirMode = 2
  FaceMakerClass = Part::FaceMakerBullseye
  LengthFwd = -18.5
  LengthRev = 0
  Solid = false
  Symmetric = false
FEATURE [Part::Part2DObjectPython] Rectangle151  # Draft 2D object (typed FeaturePython)
  ChamferSize = 0
  Columns = 1
  FilletRadius = 0
  Height = 13
  Length = 30
  MakeFace = true
  Placement = pos=(257.998,-353.852,-7.33221) rot=(1,0,0;1.5708rad)
  Rows = 1
  Support = -> [Extrude224]
FEATURE [Part::Extrusion] Extrusion036
  Base = -> Rectangle151
  Dir = (-1e-16,18.5,-4.1e-15)
  DirMode = 0
  FaceMakerClass = Part::FaceMakerBullseye
  LengthFwd = 0
  LengthRev = 0
  Solid = true
  Symmetric = false
FEATURE [Part::Cut] Cut083
  Base = -> Extrusion036
  Tool = -> Extrude224
FEATURE [Part::Part2DObjectPython] Rectangle152  # Draft 2D object (typed FeaturePython)
  ChamferSize = 0
  Columns = 1
  FilletRadius = 0
  Height = 30
  Length = 18.5
  MakeFace = true
  Placement = pos=(257.998,-353.852,-7.33221) rot=(0.707107,0.707107,0;3.14159rad)
  Rows = 1
  Support = -> [Cut083]
FEATURE [Part::Extrusion] Extrude225
  Base = -> Rectangle152
  Dir = (0,-2e-16,-1)
  DirMode = 2
  FaceMakerClass = Part::FaceMakerBullseye
  LengthFwd = 2
  LengthRev = 0
  Solid = false
  Symmetric = false
FEATURE [Part::Part2DObjectPython] Rectangle153  # Draft 2D object (typed FeaturePython)
  ChamferSize = 0
  Columns = 1
  FilletRadius = 0
  Height = 7.5
  Length = 24
  MakeFace = true
  Placement = pos=(260.998,-353.852,-5.08221) rot=(1,0,0;1.5708rad)
  Rows = 1
  Support = -> [Cut083]
FEATURE [Part::Extrusion] Extrusion037
  Base = -> Rectangle153
  Dir = (5e-16,18.5,-4.1e-15)
  DirMode = 0
  FaceMakerClass = Part::FaceMakerBullseye
  LengthFwd = 0
  LengthRev = 0
  Solid = true
  Symmetric = false
FEATURE [Part::Cut] Cut084
  Base = -> Cut083
  Tool = -> Extrusion037
FEATURE [Part::Extrusion] Extrusion038
  Base = -> Rectangle
  Dir = (-28,0,0)
  DirMode = 0
  FaceMakerClass = Part::FaceMakerBullseye
  LengthFwd = 0
  LengthRev = 0
  Solid = true
  Symmetric = false
FEATURE [Part::Cut] Cut085
  Base = -> Cut084
  Tool = -> Extrusion038
FEATURE [Part::Extrusion] Extrusion039
  Base = -> Rectangle
  Dir = (-28,0,0)
  DirMode = 0
  FaceMakerClass = Part::FaceMakerBullseye
  LengthFwd = 0
  LengthRev = 0
  Solid = true
  Symmetric = false
FEATURE [Part::MultiFuse] Fusion080
  Shapes = -> [Extrude225,Cut085]
FEATURE [Part::Feature] Face035
  Placement = pos=(286.998,-351.852,-5.08221) rot=(0.57735,0.57735,0.57735;2.0944rad)
  shape: bbox 2e-07 x 3 x 7.5 mm, 1 faces, 0 solids (baked)
FEATURE [Part::Extrusion] Extrusion040
  Base = -> Face035
  Dir = (11.952,0,0)
  DirMode = 0
  FaceMakerClass = Part::FaceMakerBullseye
  LengthFwd = 0
  LengthRev = 0
  Solid = true
  Symmetric = false
FEATURE [Part::Feature] Face037
  Placement = pos=(258.998,-351.852,-5.08221) rot=(0.57735,0.57735,0.57735;2.0944rad)
  shape: bbox 2e-07 x 3 x 7.5 mm, 1 faces, 0 solids (baked)
FEATURE [Part::Extrusion] Extrusion042
  Base = -> Face037
  Dir = (-14.0793,0,0)
  DirMode = 0
  FaceMakerClass = Part::FaceMakerBullseye
  LengthFwd = 0
  LengthRev = 0
  Solid = true
  Symmetric = false
FEATURE [Part::MultiFuse] Fusion081
  Shapes = -> [Extrusion042,Extrusion039,Extrusion040]
FEATURE [Part::Cut] Cut086
  Base = -> Fusion080
  Placement = pos=(-124.099,0,3.33221) rot=(0,0,1;0rad)
  Tool = -> Fusion081
FEATURE [Part::Part2DObjectPython] Wire  # Draft 2D object (typed FeaturePython)
  ChamferSize = 0
  Closed = true
  End = (260.998,-353.852,-5.08221)
  FilletRadius = 0
  Length = 72
  MakeFace = true
  Placement = pos=(260.998,-353.852,2.41779) rot=(1,0,0;1.5708rad)
  Points = (12) [(0,0,0),(2.5,1.33227e-15,0),(2.5,2.25,0),(21.5,2.25,0),(21.5,8.88178e-16,0),(24,4.44089e-16,0),(24,-7.5,0),(21.5,-7.5,0),(21.5,-9.75,0),(2.5,-9.75,0),(2.5,-7.5,0),(0,-7.5,0)]
  Start = (260.998,-353.852,2.41779)
  Subdivisions = 0
FEATURE [Part::Extrusion] Extrude226
  Base = -> Wire
  Dir = (0,-1,2e-16)
  DirMode = 2
  FaceMakerClass = Part::FaceMakerBullseye
  LengthFwd = 10
  LengthRev = 0
  Placement = pos=(-124.099,8.56212,3.33221) rot=(0,0,1;0rad)
  Solid = false
  Symmetric = false
FEATURE [Part::Cut] Cut087
  Base = -> Cut077
  Tool = -> Extrude226
FEATURE [Part::Part2DObjectPython] Rectangle154  # Draft 2D object (typed FeaturePython)
  ChamferSize = 0
  Columns = 1
  FilletRadius = 0
  Height = 2.5
  Length = 5.5
  MakeFace = true
  Placement = pos=(136.899,-349.102,-1.75) rot=(0,0,1;3.14159rad)
  Rows = 1
  Support = -> [Cut086]
FEATURE [Part::Extrusion] Extrusion043
  Base = -> Rectangle154
  Dir = (-1e-16,1.7e-15,6.5)
  DirMode = 0
  FaceMakerClass = Part::FaceMakerBullseye
  LengthFwd = 0
  LengthRev = 0
  Placement = pos=(-1.99999,0,0.5) rot=(0,0,1;0rad)
  Solid = true
  Symmetric = false
FEATURE [Part::Feature] Face038
  Placement = pos=(134.899,-349.102,5.25) rot=(0,0,1;3.14159rad)
  shape: bbox 5.5 x 2.5 x 2e-07 mm, 1 faces, 0 solids (baked)
FEATURE [Part::Extrusion] Extrusion044
  Base = -> Face038
  Dir = (0,1e-16,0.5)
  DirMode = 0
  FaceMakerClass = Part::FaceMakerBullseye
  LengthFwd = 0
  LengthRev = 0
  Solid = true
  Symmetric = false
FEATURE [Part::MultiFuse] Fusion082
  Placement = pos=(0,0,-0.25) rot=(0,0,1;0rad)
  Shapes = -> [Extrusion043,Extrusion044]
FEATURE [Part::Feature] Face039
  Placement = pos=(0,0,-0.25) rot=(0,0,1;0rad)
  shape: bbox 2e-07 x 2.5 x 0.5 mm, 1 faces, 0 solids (baked)
FEATURE [Part::Extrusion] Extrusion045
  Base = -> Face039
  Dir = (2.49999,0,0)
  DirMode = 0
  FaceMakerClass = Part::FaceMakerBullseye
  LengthFwd = 0
  LengthRev = 0
  Solid = true
  Symmetric = false
FEATURE [Part::Feature] Face040
  Placement = pos=(0,0,-0.25) rot=(0,0,1;0rad)
  shape: bbox 2e-07 x 2.5 x 6.5 mm, 1 faces, 0 solids (baked)
FEATURE [Part::Extrusion] Extrusion046
  Base = -> Face040
  Dir = (2.49999,0,0)
  DirMode = 0
  FaceMakerClass = Part::FaceMakerBullseye
  LengthFwd = 0
  LengthRev = 0
  Solid = true
  Symmetric = false
FEATURE [Part::Cut] Cut088
  Base = -> Fusion082
  Tool = -> Extrusion045
FEATURE [Part::Cut] Cut089
  Base = -> Cut088
  Tool = -> Extrusion046
FEATURE [Part::Part2DObjectPython] Rectangle157  # Draft 2D object (typed FeaturePython)
  ChamferSize = 0
  Columns = 1
  FilletRadius = 0
  Height = 7
  Length = 2.5
  MakeFace = true
  Placement = pos=(162.899,-349.102,-1.5) rot=(0.57735,-0.57735,-0.57735;2.0944rad)
  Rows = 1
  Support = -> [Cut089]
FEATURE [Part::Extrusion] Extrude227
  Base = -> Rectangle157
  Dir = (-1,-2e-16,-2e-16)
  DirMode = 2
  FaceMakerClass = Part::FaceMakerBullseye
  LengthFwd = -3
  LengthRev = 0
  Solid = false
  Symmetric = false
FEATURE [Part::Part2DObjectPython] Rectangle159  # Draft 2D object (typed FeaturePython)
  ChamferSize = 0
  Columns = 1
  FilletRadius = 0
  Height = 14.3
  Length = 1
  MakeFace = true
  Placement = pos=(166.939,-349.382,5.5) rot=(0,0,1;0.283123rad)
  Rows = 1
FEATURE [Part::Part2DObjectPython] Rectangle160  # Draft 2D object (typed FeaturePython)
  ChamferSize = 0
  Columns = 1
  FilletRadius = 0
  Height = 14.3
  Length = 0.88
  MakeFace = true
  Placement = pos=(129.899,-349.102,5.5) rot=(0,0,-1;0.283566rad)
  Rows = 1
FEATURE [Part::Part2DObjectPython] Rectangle161  # Draft 2D object (typed FeaturePython)
  ChamferSize = 0
  Columns = 1
  FilletRadius = 0
  Height = 15
  Length = 30
  MakeFace = true
  Placement = pos=(133.899,-335.352,9) rot=(-1,0,0;1.5708rad)
  Rows = 1
  Support = -> [Cut086]
FEATURE [Part::Extrusion] Extrude228
  Base = -> Rectangle161
  Dir = (0,1,2e-16)
  DirMode = 2
  FaceMakerClass = Part::FaceMakerBullseye
  LengthFwd = 1
  LengthRev = 0
  Solid = false
  Symmetric = false
FEATURE [Part::Part2DObjectPython] Circle057  # Draft 2D object (typed FeaturePython)
  FirstAngle = 0
  LastAngle = 0
  MakeFace = true
  Placement = pos=(156.399,-335.352,2) rot=(1,0,0;1.5708rad)
  Radius = 1.5
FEATURE [Part::Part2DObjectPython] Circle058  # Draft 2D object (typed FeaturePython)
  FirstAngle = 0
  LastAngle = 0
  MakeFace = true
  Placement = pos=(141.399,-335.352,2) rot=(1,0,0;1.5708rad)
  Radius = 1.5
FEATURE [Part::Extrusion] Extrude229
  Base = -> Circle057
  Dir = (0,-1,-2e-16)
  DirMode = 2
  FaceMakerClass = Part::FaceMakerBullseye
  LengthFwd = -2
  LengthRev = 0
  Solid = false
  Symmetric = false
FEATURE [Part::Extrusion] Extrude230
  Base = -> Circle058
  Dir = (0,-1,-2e-16)
  DirMode = 2
  FaceMakerClass = Part::FaceMakerBullseye
  LengthFwd = -2
  LengthRev = 0
  Solid = false
  Symmetric = false
FEATURE [Part::Cut] Cut090
  Base = -> Extrude228
  Tool = -> Extrude229
FEATURE [Part::Feature] Face044
  Placement = pos=(-124.099,0,3.33221) rot=(0,0,1;0rad)
  shape: bbox 19 x 18.5 x 2e-07 mm, 1 faces, 0 solids (baked)
FEATURE [Part::Extrusion] Extrusion052
  Base = -> Face044
  Dir = (0,0,-0.2)
  DirMode = 0
  FaceMakerClass = Part::FaceMakerBullseye
  LengthFwd = 0
  LengthRev = 0
  Solid = true
  Symmetric = false
FEATURE [Part::Part2DObjectPython] Rectangle162  # Draft 2D object (typed FeaturePython)
  ChamferSize = 0
  Columns = 1
  FilletRadius = 0
  Height = 0.2
  Length = 19
  MakeFace = true
  Placement = pos=(139.399,-353.852,-4.2) rot=(1,0,0;1.5708rad)
  Rows = 1
FEATURE [Part::Extrusion] Extrude231
  Base = -> Rectangle162
  Dir = (-3e-16,-1,2e-16)
  DirMode = 2
  FaceMakerClass = Part::FaceMakerBullseye
  LengthFwd = 10
  LengthRev = 0
  Placement = pos=(0,5,-9e-16) rot=(0,0,1;0rad)
  Solid = false
  Symmetric = false
FEATURE [Part::Cut] Cut093
  Base = -> Cut087
  Tool = -> Extrude231
FEATURE [Part::Part2DObjectPython] Circle059  # Draft 2D object (typed FeaturePython)
  FirstAngle = 0
  LastAngle = 0
  MakeFace = true
  Placement = pos=(-124.786,-399.051,-9) rot=(1,0,0;3.14157rad)
  Radius = 6
FEATURE [Part::Extrusion] Extrusion053
  Base = -> Circle059
  Dir = (0,4.38557e-05,2)
  DirMode = 0
  FaceMakerClass = Part::FaceMakerBullseye
  LengthFwd = 0
  LengthRev = 0
  Placement = pos=(3.77685,28.445,-0.000623738) rot=(0,0,1;0rad)
  Solid = true
  Symmetric = false
FEATURE [Part::Part2DObjectPython] Circle060  # Draft 2D object (typed FeaturePython)
  FirstAngle = 0
  LastAngle = 0
  MakeFace = true
  Placement = pos=(-121.009,-370.606,-7.00062) rot=(-1,0,0;2.2e-05rad)
  Radius = 2.5
  Support = -> [Cut049]
FEATURE [Part::Extrusion] Extrude232
  Base = -> Circle060
  Dir = (0,2.19278e-05,1)
  DirMode = 2
  FaceMakerClass = Part::FaceMakerBullseye
  LengthFwd = 2.3
  LengthRev = 0
  Solid = false
  Symmetric = false
FEATURE [Part::Part2DObjectPython] Circle061  # Draft 2D object (typed FeaturePython)
  FirstAngle = 0
  LastAngle = 0
  MakeFace = true
  Placement = pos=(-121.009,-370.606,-4.70062) rot=(-1,0,0;2.2e-05rad)
  Radius = 1.4
FEATURE [Part::Extrusion] Extrude233
  Base = -> Circle061
  Dir = (0,2.19278e-05,1)
  DirMode = 2
  FaceMakerClass = Part::FaceMakerBullseye
  LengthFwd = -3.3
  LengthRev = 0
  Solid = false
  Symmetric = false
FEATURE [Part::MultiFuse] Fusion085
  Shapes = -> [Extrusion053,Extrude232]
FEATURE [Part::Cut] Cut094
  Base = -> Fusion085
  Tool = -> Extrude233
FEATURE [Part::Part2DObjectPython] Circle062  # Draft 2D object (typed FeaturePython)
  FirstAngle = 0
  LastAngle = 0
  MakeFace = true
  Placement = pos=(-137.596,-370.962,-9.00062) rot=(1,0,0;3.14157rad)
  Radius = 3
FEATURE [Part::Extrusion] Extrude234
  Base = -> Circle062
  Dir = (0,-2.19278e-05,-1)
  DirMode = 2
  FaceMakerClass = Part::FaceMakerBullseye
  LengthFwd = 2
  LengthRev = 0
  Placement = pos=(-4.4885,0.937158,1.99998) rot=(0,0,1;0rad)
  Solid = false
  Symmetric = false
FEATURE [Part::Part2DObjectPython] Circle063  # Draft 2D object (typed FeaturePython)
  FirstAngle = 0
  LastAngle = 0
  MakeFace = true
  Placement = pos=(-142.085,-370.025,-7.00064) rot=(1,0,0;3.14157rad)
  Radius = 1.5
  Support = -> [Extrude234]
FEATURE [Part::Extrusion] Extrude235
  Base = -> Circle063
  Dir = (0,-2.19278e-05,-1)
  DirMode = 2
  FaceMakerClass = Part::FaceMakerBullseye
  LengthFwd = 3
  LengthRev = 0
  Solid = false
  Symmetric = false
FEATURE [Part::Cut] Cut095
  Base = -> Extrude234
  Placement = pos=(9.23743,-0.707609,1.55163e-05) rot=(0,0,1;0rad)
  Tool = -> Extrude235
FEATURE [Part::Cut] Cut096
  Base = -> Cut090
  Placement = pos=(-5.62499,0,0) rot=(0,0,1;0rad)
  Tool = -> Extrude230
FEATURE [Part::Cut] Cut097
  Base = -> Cut086
  Tool = -> Extrusion052
FEATURE [Part::Feature] Face045
  Placement = pos=(-124.099,0,3.33221) rot=(0,0,1;0rad)
  shape: bbox 2 x 3e-07 x 7.5 mm, 1 faces, 0 solids (baked)
FEATURE [Part::Feature] Face047
  Placement = pos=(-124.099,0,3.33221) rot=(0,0,1;0rad)
  shape: bbox 2 x 3e-07 x 7.5 mm, 1 faces, 0 solids (baked)
FEATURE [Part::Extrusion] Extrusion054
  Base = -> Face047
  Dir = (0,-0.400003,0)
  DirMode = 0
  FaceMakerClass = Part::FaceMakerBullseye
  LengthFwd = 0
  LengthRev = 0
  Solid = true
  Symmetric = false
FEATURE [Part::Cut] Cut098
  Base = -> Cut097
  Tool = -> Extrusion054
FEATURE [Part::Extrusion] Extrusion055
  Base = -> Face045
  Dir = (0,-0.400003,0)
  DirMode = 0
  FaceMakerClass = Part::FaceMakerBullseye
  LengthFwd = 0
  LengthRev = 0
  Solid = true
  Symmetric = false
FEATURE [Part::Cut] Cut099
  Base = -> Cut098
  Tool = -> Extrusion055
FEATURE [Part::Part2DObjectPython] Rectangle163  # Draft 2D object (typed FeaturePython)
  ChamferSize = 0
  Columns = 1
  FilletRadius = 0
  Height = 7
  Length = 2.5
  MakeFace = true
  Placement = pos=(165.899,-351.602,-1.5) rot=(0.57735,0.57735,0.57735;2.0944rad)
  Rows = 1
  Support = -> [Extrude227]
FEATURE [Part::Extrusion] Extrude236
  Base = -> Rectangle163
  Dir = (1,0,0)
  DirMode = 2
  FaceMakerClass = Part::FaceMakerBullseye
  LengthFwd = 2
  LengthRev = 0
  Solid = false
  Symmetric = false
FEATURE [Part::Part2DObjectPython] Rectangle164  # Draft 2D object (typed FeaturePython)
  ChamferSize = 0
  Columns = 1
  FilletRadius = 0
  Height = 7
  Length = 2.5
  MakeFace = true
  Placement = pos=(131.899,-351.602,-1.5) rot=(0.57735,0.57735,0.57735;2.0944rad)
  Rows = 1
FEATURE [Part::Extrusion] Extrude237
  Base = -> Rectangle164
  Dir = (1,0,0)
  DirMode = 2
  FaceMakerClass = Part::FaceMakerBullseye
  LengthFwd = -2
  LengthRev = 0
  Solid = false
  Symmetric = false
FEATURE [Part::Extrusion] Extrusion056
  Base = -> Rectangle159
  Dir = (1e-16,-2.1e-15,-7)
  DirMode = 0
  FaceMakerClass = Part::FaceMakerBullseye
  LengthFwd = 0
  LengthRev = 0
  Solid = true
  Symmetric = false
FEATURE [Part::Extrusion] Extrusion057
  Base = -> Rectangle160
  Dir = (0,-2.1e-15,-7)
  DirMode = 0
  FaceMakerClass = Part::FaceMakerBullseye
  LengthFwd = 0
  LengthRev = 0
  Solid = true
  Symmetric = false
FEATURE [Part::MultiFuse] Fusion086
  Shapes = -> [Cut089,Extrude237,Extrusion057,Extrude227,Extrude236,Extrusion056]
FEATURE [Part::MultiFuse] Fusion087
  Placement = pos=(39.6248,-78.9998,3.6e-15) rot=(0,0,1;0rad)
  Shapes = -> [Fusion086,Cut099]
FEATURE [Part::Part2DObjectPython] Rectangle166  # Draft 2D object (typed FeaturePython)
  ChamferSize = 0
  Columns = 1
  FilletRadius = 0
  Height = 28
  Length = 3.4
  MakeFace = true
  Placement = pos=(162.899,-352.252,-1.75) rot=(0,0,1;1.5708rad)
  Rows = 1
FEATURE [Part::Extrusion] Extrusion058
  Base = -> Rectangle166
  Dir = (-1.39748e-07,1.39748e-07,7.5)
  DirMode = 0
  FaceMakerClass = Part::FaceMakerBullseye
  LengthFwd = 0
  LengthRev = 0
  Solid = true
  Symmetric = false
FEATURE [Part::Cut] Cut100
  Base = -> Cut093
  Tool = -> Extrusion058
FEATURE [Part::Part2DObjectPython] Rectangle167  # Draft 2D object (typed FeaturePython)
  ChamferSize = 0
  Columns = 1
  FilletRadius = 0
  Height = 16
  Length = 50
  MakeFace = true
  Placement = pos=(118.274,-361.852,9) rot=(0,0,1;0rad)
  Rows = 1
  Support = -> [Cut100]
FEATURE [Part::Extrusion] Extrude238
  Base = -> Rectangle167
  Dir = (0,0,1)
  DirMode = 2
  FaceMakerClass = Part::FaceMakerBullseye
  LengthFwd = -40
  LengthRev = 0
  Solid = false
  Symmetric = false
FEATURE [Part::Cut] Cut101
  Base = -> Cut100
  Tool = -> Extrude238
FEATURE [Part::Feature] Face048
  shape: bbox 4e-07 x 5 x 18 mm, 1 faces, 0 solids (baked)
FEATURE [Part::Extrusion] Extrusion059
  Base = -> Face048
  Dir = (50,1.5e-15,0)
  DirMode = 0
  FaceMakerClass = Part::FaceMakerBullseye
  LengthFwd = 0
  LengthRev = 0
  Solid = true
  Symmetric = false
FEATURE [Part::MultiFuse] Fusion088
  Shapes = -> [Cut101,Extrusion059]
FEATURE [Part::Feature] Face049
  Placement = pos=(39.6248,-78.9998,3.6e-15) rot=(0,0,1;0rad)
  shape: bbox 1 x 3e-07 x 7.5 mm, 1 faces, 0 solids (baked)
FEATURE [Part::Extrusion] Extrusion060
  Base = -> Face049
  Dir = (0,-0.300003,0)
  DirMode = 0
  FaceMakerClass = Part::FaceMakerBullseye
  LengthFwd = 0
  LengthRev = 0
  Solid = true
  Symmetric = false
FEATURE [Part::Cut] Cut102
  Base = -> Fusion087
  Tool = -> Extrusion060
FEATURE [Part::Feature] Face050
  Placement = pos=(39.6248,-78.9998,3.6e-15) rot=(0,0,1;0rad)
  shape: bbox 1 x 3e-07 x 7.5 mm, 1 faces, 0 solids (baked)
FEATURE [Part::Extrusion] Extrusion061
  Base = -> Face050
  Dir = (0,-0.300003,0)
  DirMode = 0
  FaceMakerClass = Part::FaceMakerBullseye
  LengthFwd = 0
  LengthRev = 0
  Solid = true
  Symmetric = false
FEATURE [Part::Cut] Cut103
  Base = -> Cut102
  Placement = pos=(-45.2498,78.9998,9e-16) rot=(0,0,1;0rad)
  Tool = -> Extrusion061
FEATURE [Part::Part2DObjectPython] Rectangle168  # Draft 2D object (typed FeaturePython)
  ChamferSize = 0
  Columns = 1
  FilletRadius = 0
  Height = 30
  Length = 18.5
  MakeFace = true
  Placement = pos=(275.392,-497.324,9) rot=(0,0,1;1.5708rad)
  Rows = 1
  Support = -> [Cut103]
FEATURE [Part::Extrusion] Extrusion062
  Base = -> Rectangle168
  Dir = (2e-16,-3.1e-15,-15)
  DirMode = 0
  FaceMakerClass = Part::FaceMakerBullseye
  LengthFwd = 0
  LengthRev = 0
  Placement = pos=(-117.118,143.472,0) rot=(0,0,1;0rad)
  Solid = true
  Symmetric = false
FEATURE [Part::Cut] Cut104
  Base = -> Fusion088
  Tool = -> Extrusion062
FEATURE [Part::Feature] Fusion076001  label="Fusion091"
  Placement = pos=(-6.79071,-148.437,16) rot=(0,0,1;0rad)
  shape: bbox 204 x 104 x 6 mm, 190 faces, 2 solids (baked)
FEATURE [Part::MultiFuse] Fusion076002
  Shapes = -> [Cut103,Cut096]
FEATURE [Part::Feature] Fusion076002_solid  label="Solid-Socket.Block-230V"
  Placement = pos=(-220.143,-31.4219,-14) rot=(0,0,1;0rad)
  shape: bbox 38 x 19.5 x 15 mm, 102 faces (baked)
FEATURE [Part::Feature] Face051
  Placement = pos=(-5.62499,0,-0.25) rot=(0,0,1;0rad)
  shape: bbox 2e-07 x 2.5 x 6.5 mm, 1 faces, 0 solids (baked)
FEATURE [Part::Extrusion] Extrusion063
  Base = -> Face051
  Dir = (1,0,0)
  DirMode = 0
  FaceMakerClass = Part::FaceMakerBullseye
  LengthFwd = 0
  LengthRev = 0
  Solid = true
  Symmetric = false
FEATURE [Part::Feature] Face052
  Placement = pos=(157.274,-349.102,-1.5) rot=(0.57735,-0.57735,-0.57735;2.0944rad)
  shape: bbox 2e-07 x 2.5 x 7 mm, 1 faces, 0 solids (baked)
FEATURE [Part::Extrusion] Extrusion064
  Base = -> Face052
  Dir = (-1,0,0)
  DirMode = 0
  FaceMakerClass = Part::FaceMakerBullseye
  LengthFwd = 0
  LengthRev = 0
  Solid = true
  Symmetric = false
FEATURE [Part::MultiFuse] Fusion076003
  Shapes = -> [Extrusion064,Extrusion063,Fusion076002]
FEATURE [Part::MultiFuse] Fusion076004
  Shapes = -> [Cut104,Fusion076003]
